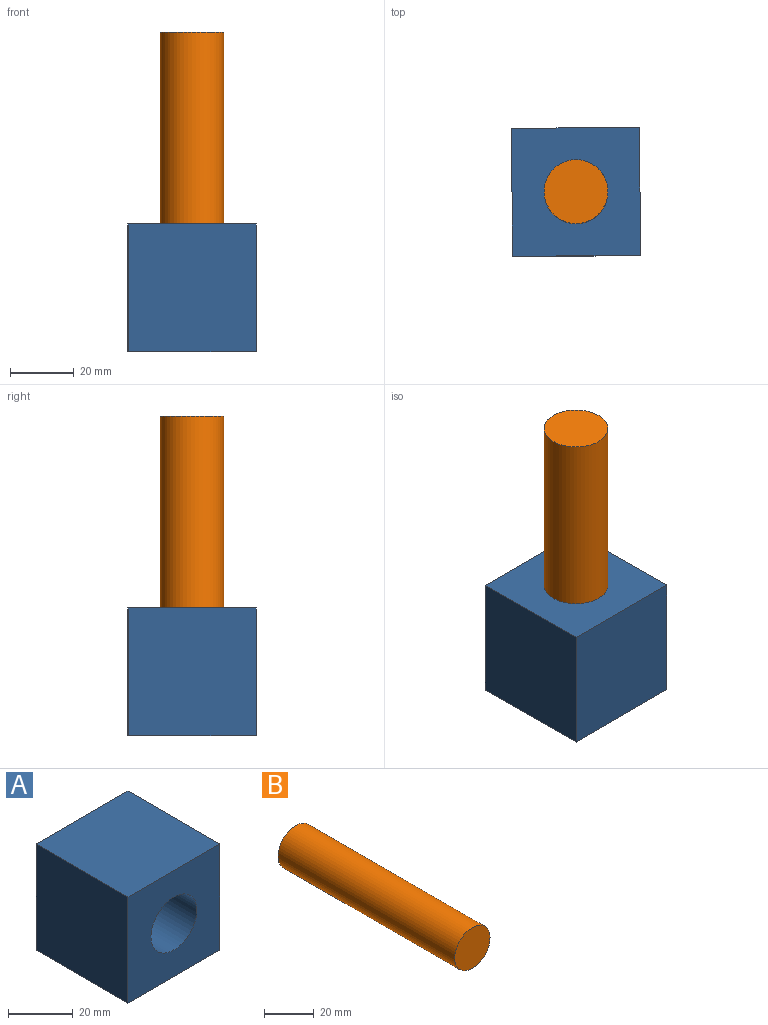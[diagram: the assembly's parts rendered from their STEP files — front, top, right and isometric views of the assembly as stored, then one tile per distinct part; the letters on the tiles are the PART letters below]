
ASSEMBLY  parts=2 mates=1
PART A: 7 faces, bbox 40x40x40 mm
  f0: plane 40x40mm, normal (1,0,0), area 1600mm2, adj f1,f3,f5,f6
  f1: plane 40x40mm, normal (0,0,1), area 1600mm2, adj f0,f2,f5,f6
  f2: plane 40x40mm, normal (-1,0,0), area 1600mm2, adj f1,f3,f5,f6
  f3: plane 40x40mm, normal (0,0,-1), area 1600mm2, adj f0,f2,f5,f6
  f4: cylinder r=10mm len=40mm, axis (0,1,0), area 2513.3mm2, adj f5,f6
  f5: plane 40x40mm, normal (0,-1,0), area 1285.8mm2, adj f0,f1,f2,f3,f4
  f6: plane 40x40mm, normal (0,1,0), area 1285.8mm2, adj f0,f1,f2,f3,f4
PART B: 3 faces, bbox 20x100x20 mm
  f0: cylinder r=10mm len=100mm, axis (0,1,0), area 6283.2mm2, adj f1,f2
  f1: plane 20x20mm, normal (0,-1,0), area 314.2mm2, adj f0
  f2: plane 20x20mm, normal (0,1,0), area 314.2mm2, adj f0
PLACE A rot(axis=(-0.58,0.58,-0.58),119.8deg) t=(0,0,-100)mm
PLACE B rot(axis=(-1,0,0),90deg) t=(0,0,-100)mm
MATE cylindrical A.f4 <-> B.f0  axis (0,0,-1) through (0,0,-60)mm
